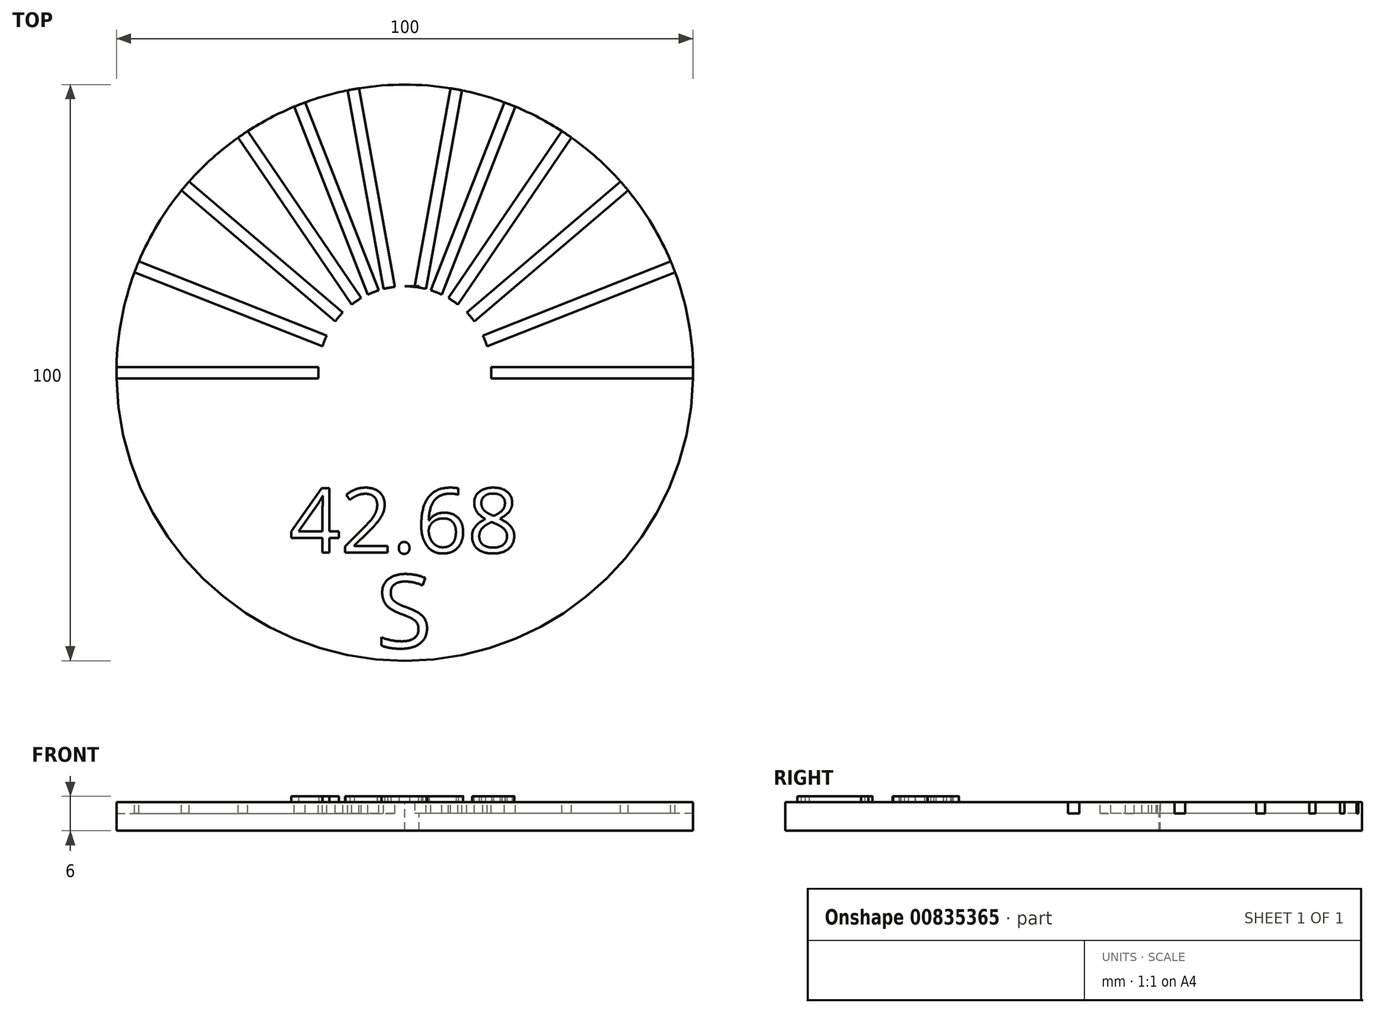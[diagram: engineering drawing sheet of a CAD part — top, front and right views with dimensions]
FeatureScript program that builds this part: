
annotation { "Feature Type Name" : "Feature", "Feature Type Description" : "" }
export const myFeature = defineFeature(function(context is Context, id is Id, definition is map)
    precondition{}
    {
        {
            var Q0;
            Q0=qCreatedBy(makeId("Top.planeOp"),FACE);
            var sketch = newSketch(context, id + "F0", { "sketchPlane" : qUnion([Q0])});
            skCircle(sketch, "E0", {"center": v(0, 0) * mm, "radius": 50 * mm});
            skSolve(sketch);
        }
        {
            var Q0;
            Q0 = qSketchRegion(id + "F0", true);
            extrude(context, id + "F1", {"entities" : qUnion([Q0]), "depth" : 5 * mm, "offsetDistance" : 25 * mm});
        }
        {
            var Q0;
            Q0=makeQuery(id+"F1.opExtrude","CAP_FACE",FACE,{"disambiguationData":[OSD([sQuery(id+"F0.wireOp",EDGE,"E0")])],"isStart":false});
            var sketch = newSketch(context, id + "F2", { "sketchPlane" : qUnion([Q0])});
            skCircle(sketch, "E1", {"center": v(0, 0) * mm, "radius": 15 * mm});
            skLineSegment(sketch, "E2", {"start": v(-50, 0) * mm, "end": v(0, 0) * mm, "construction": true});
            skLineSegment(sketch, "E3", {"start": v(-49.99, 1) * mm, "end": v(-14.97, 1) * mm});
            skLineSegment(sketch, "E4", {"start": v(-49.99, -1) * mm, "end": v(-14.97, -1) * mm});
            skPoint(sketch, "E5", {"position": v(-46.5, 18.38) * mm});
            skLineSegment(sketch, "E6", {"start": v(-46.5, 18.38) * mm, "end": v(0, 0) * mm, "construction": true});
            skLineSegment(sketch, "E7", {"start": v(-46.12, 19.3) * mm, "end": v(-13.55, 6.43) * mm});
            skLineSegment(sketch, "E8", {"start": v(-46.86, 17.45) * mm, "end": v(-14.29, 4.57) * mm});
            skLineSegment(sketch, "E9", {"start": v(-38.07, 32.42) * mm, "end": v(0, 0) * mm, "construction": true});
            skLineSegment(sketch, "E10", {"start": v(-37.4, 33.17) * mm, "end": v(-10.75, 10.47) * mm});
            skLineSegment(sketch, "E11", {"start": v(-38.7, 31.65) * mm, "end": v(-12.04, 8.94) * mm});
            skLineSegment(sketch, "E12", {"start": v(-28.05, 41.39) * mm, "end": v(0, 0) * mm, "construction": true});
            skLineSegment(sketch, "E13", {"start": v(-27.22, 41.94) * mm, "end": v(-7.57, 12.95) * mm});
            skLineSegment(sketch, "E14", {"start": v(-28.88, 40.82) * mm, "end": v(-9.23, 11.83) * mm});
            skLineSegment(sketch, "E15", {"start": v(-18.22, 46.56) * mm, "end": v(0, 0) * mm, "construction": true});
            skLineSegment(sketch, "E16", {"start": v(-19.15, 46.19) * mm, "end": v(-6.38, 13.57) * mm});
            skLineSegment(sketch, "E17", {"start": v(-17.28, 46.92) * mm, "end": v(-4.52, 14.3) * mm});
            skLineSegment(sketch, "E18", {"start": v(-8.94, 49.2) * mm, "end": v(0, 0) * mm, "construction": true});
            skLineSegment(sketch, "E19", {"start": v(-7.95, 49.36) * mm, "end": v(-1.7, 14.9) * mm});
            skLineSegment(sketch, "E20", {"start": v(-9.92, 49) * mm, "end": v(-3.66, 14.55) * mm});
            skLineSegment(sketch, "E21", {"start": v(50, 0) * mm, "end": v(0, 0) * mm, "construction": true});
            skLineSegment(sketch, "E22", {"start": v(49.99, 1) * mm, "end": v(14.97, 1) * mm});
            skLineSegment(sketch, "E23", {"start": v(49.99, -1) * mm, "end": v(14.97, -1) * mm});
            skLineSegment(sketch, "E24", {"start": v(46.5, 18.38) * mm, "end": v(0, 0) * mm, "construction": true});
            skLineSegment(sketch, "E25", {"start": v(46.86, 17.45) * mm, "end": v(14.29, 4.57) * mm});
            skLineSegment(sketch, "E26", {"start": v(46.12, 19.3) * mm, "end": v(13.55, 6.43) * mm});
            skLineSegment(sketch, "E27", {"start": v(38.07, 32.42) * mm, "end": v(0, 0) * mm, "construction": true});
            skLineSegment(sketch, "E28", {"start": v(38.7, 31.65) * mm, "end": v(12.04, 8.94) * mm});
            skLineSegment(sketch, "E29", {"start": v(37.4, 33.17) * mm, "end": v(10.75, 10.47) * mm});
            skLineSegment(sketch, "E30", {"start": v(28.05, 41.39) * mm, "end": v(0, 0) * mm, "construction": true});
            skLineSegment(sketch, "E31", {"start": v(28.88, 40.82) * mm, "end": v(9.23, 11.83) * mm});
            skLineSegment(sketch, "E32", {"start": v(27.22, 41.94) * mm, "end": v(7.57, 12.95) * mm});
            skLineSegment(sketch, "E33", {"start": v(18.22, 46.56) * mm, "end": v(0, 0) * mm, "construction": true});
            skLineSegment(sketch, "E34", {"start": v(19.15, 46.19) * mm, "end": v(6.38, 13.57) * mm});
            skLineSegment(sketch, "E35", {"start": v(17.28, 46.92) * mm, "end": v(4.52, 14.3) * mm});
            skLineSegment(sketch, "E36", {"start": v(8.94, 49.2) * mm, "end": v(0, 0) * mm, "construction": true});
            skLineSegment(sketch, "E37", {"start": v(9.92, 49) * mm, "end": v(3.66, 14.55) * mm});
            skLineSegment(sketch, "E38", {"start": v(7.95, 49.36) * mm, "end": v(1.7, 14.9) * mm});
            skSolve(sketch);
        }
        {
            var Q0;
            {var subQ0=sQuery(id+"F2.wireOp",EDGE,"E3");Q0=makeQuery(id+"F2.imprint","IMPRINT",FACE,{"disambiguationData":[TD([[makeQuery(id+"F2.imprint","IMPRINT",EDGE,{"derivedFrom":subQ0}),-1.0]])]});}
            var Q1;
            {var subQ0=sQuery(id+"F2.wireOp",EDGE,"E7");Q1=makeQuery(id+"F2.imprint","IMPRINT",FACE,{"disambiguationData":[TD([[makeQuery(id+"F2.imprint","IMPRINT",EDGE,{"derivedFrom":subQ0}),-1.0]])]});}
            var Q2;
            {var subQ0=sQuery(id+"F2.wireOp",EDGE,"E10");Q2=makeQuery(id+"F2.imprint","IMPRINT",FACE,{"disambiguationData":[TD([[makeQuery(id+"F2.imprint","IMPRINT",EDGE,{"derivedFrom":subQ0}),-1.0]])]});}
            var Q3;
            {var subQ0=sQuery(id+"F2.wireOp",EDGE,"E13");Q3=makeQuery(id+"F2.imprint","IMPRINT",FACE,{"disambiguationData":[TD([[makeQuery(id+"F2.imprint","IMPRINT",EDGE,{"derivedFrom":subQ0}),-1.0]])]});}
            var Q4;
            {var subQ0=sQuery(id+"F2.wireOp",EDGE,"E16");Q4=makeQuery(id+"F2.imprint","IMPRINT",FACE,{"disambiguationData":[TD([[makeQuery(id+"F2.imprint","IMPRINT",EDGE,{"derivedFrom":subQ0}),1.0]])]});}
            var Q5;
            {var subQ0=sQuery(id+"F2.wireOp",EDGE,"E19");Q5=makeQuery(id+"F2.imprint","IMPRINT",FACE,{"disambiguationData":[TD([[makeQuery(id+"F2.imprint","IMPRINT",EDGE,{"derivedFrom":subQ0}),-1.0]])]});}
            var Q6;
            {var subQ0=sQuery(id+"F2.wireOp",EDGE,"cLizcYDV-IRRK-Rsa2-aBVT-mdBlfsuyFpmo");Q6=makeQuery(id+"F2.imprint","IMPRINT",FACE,{"disambiguationData":[TD([[makeQuery(id+"F2.imprint","IMPRINT",EDGE,{"derivedFrom":subQ0}),1.0]])]});}
            var Q7;
            {var subQ0=sQuery(id+"F2.wireOp",EDGE,"E37");Q7=makeQuery(id+"F2.imprint","IMPRINT",FACE,{"disambiguationData":[TD([[makeQuery(id+"F2.imprint","IMPRINT",EDGE,{"derivedFrom":subQ0}),-1.0]])]});}
            var Q8;
            {var subQ0=sQuery(id+"F2.wireOp",EDGE,"E34");Q8=makeQuery(id+"F2.imprint","IMPRINT",FACE,{"disambiguationData":[TD([[makeQuery(id+"F2.imprint","IMPRINT",EDGE,{"derivedFrom":subQ0}),-1.0]])]});}
            var Q9;
            {var subQ0=sQuery(id+"F2.wireOp",EDGE,"E31");Q9=makeQuery(id+"F2.imprint","IMPRINT",FACE,{"disambiguationData":[TD([[makeQuery(id+"F2.imprint","IMPRINT",EDGE,{"derivedFrom":subQ0}),-1.0]])]});}
            var Q10;
            {var subQ0=sQuery(id+"F2.wireOp",EDGE,"E28");Q10=makeQuery(id+"F2.imprint","IMPRINT",FACE,{"disambiguationData":[TD([[makeQuery(id+"F2.imprint","IMPRINT",EDGE,{"derivedFrom":subQ0}),-1.0]])]});}
            var Q11;
            {var subQ0=sQuery(id+"F2.wireOp",EDGE,"E25");Q11=makeQuery(id+"F2.imprint","IMPRINT",FACE,{"disambiguationData":[TD([[makeQuery(id+"F2.imprint","IMPRINT",EDGE,{"derivedFrom":subQ0}),-1.0]])]});}
            var Q12;
            {var subQ0=sQuery(id+"F2.wireOp",EDGE,"E22");Q12=makeQuery(id+"F2.imprint","IMPRINT",FACE,{"disambiguationData":[TD([[makeQuery(id+"F2.imprint","IMPRINT",EDGE,{"derivedFrom":subQ0}),1.0]])]});}
            extrude(context, id + "F3", {"entities" : qUnion([Q0, Q1, Q2, Q3, Q4, Q5, Q6, Q7, Q8, Q9, Q10, Q11, Q12]), "operationType" : NewBodyOperationType.REMOVE, "oppositeDirection" : true, "depth" : 2 * mm, "offsetDistance" : 25 * mm});
        }
        {
            var Q0;
            Q0=makeQuery(id+"F1.opExtrude","CAP_FACE",FACE,{"disambiguationData":[OSD([sQuery(id+"F0.wireOp",EDGE,"E0")])],"isStart":false});
            var sketch = newSketch(context, id + "F4", { "sketchPlane" : qUnion([Q0])});
            skCircle(sketch, "E39", {"center": v(0, 0) * mm, "radius": 15 * mm});
            skSolve(sketch);
        }
        {
            var Q0;
            {var subQ0=sQuery(id+"F0.wireOp",EDGE,"E0");Q0=makeQuery(id+"FESnY8lzPuoSr7a_1.boolean.opBoolean","SPLIT",FACE,{"disambiguationData":[TD([makeQuery(id+"F3.boolean.opBoolean","COPY",FACE,{"derivedFrom":makeQuery(id+"F3.opExtrude","SWEPT_FACE",FACE,{"disambiguationData":[OSD([sQuery(id+"F2.wireOp",EDGE,"E4")])]})})])],"derivedFrom":makeQuery(id+"F1.opExtrude","CAP_FACE",FACE,{"disambiguationData":[OSD([subQ0])],"isStart":false})});}
            var sketch = newSketch(context, id + "F5", { "sketchPlane" : qUnion([Q0])});
            skText(sketch, "E40", { "text": "S", "fontName": "OpenSans-Regular.ttf"});
            const initialGuessF5  = {"E40": [-0.005, -0.04773, 1, 0, 0.01273]};
            skSetInitialGuess(sketch, initialGuessF5);
            skSolve(sketch);
        }
        {
            var Q0;
            Q0 = qSketchRegion(id + "F5", true);
            extrude(context, id + "F6", {"entities" : qUnion([Q0]), "operationType" : NewBodyOperationType.ADD, "depth" : 1 * mm, "offsetDistance" : 25 * mm});
        }
        {
            var Q0;
            {var subQ0=sQuery(id+"F0.wireOp",EDGE,"E0");Q0=makeQuery(id+"FESnY8lzPuoSr7a_1.boolean.opBoolean","SPLIT",FACE,{"disambiguationData":[TD([makeQuery(id+"F3.boolean.opBoolean","COPY",FACE,{"derivedFrom":makeQuery(id+"F3.opExtrude","SWEPT_FACE",FACE,{"disambiguationData":[OSD([sQuery(id+"F2.wireOp",EDGE,"E4")])]})})])],"derivedFrom":makeQuery(id+"F1.opExtrude","CAP_FACE",FACE,{"disambiguationData":[OSD([subQ0])],"isStart":false})});}
            var sketch = newSketch(context, id + "F7", { "sketchPlane" : qUnion([Q0])});
            skText(sketch, "E41", { "text": "42.68", "fontName": "OpenSans-Regular.ttf"});
            const initialGuessF7  = {"E41": [-0.02, -0.03122, 1, 0, 0.01122]};
            skSetInitialGuess(sketch, initialGuessF7);
            skSolve(sketch);
        }
        {
            var Q0;
            Q0 = qSketchRegion(id + "F7", true);
            extrude(context, id + "F8", {"entities" : qUnion([Q0]), "operationType" : NewBodyOperationType.ADD, "depth" : 1 * mm, "offsetDistance" : 25 * mm});
        }
        {
            var Q0;
            {var subQ0=sQuery(id+"F4.wireOp",EDGE,"E39");var subQ18=makeQuery(id+"F4.imprint","INTERSECT",VERTEX,{"derivedFrom":[makeQuery(id+"F3.boolean.opBoolean","COPY",EDGE,{"derivedFrom":makeQuery(id+"F3.opExtrude","CAP_EDGE",EDGE,{"disambiguationData":[OSD([sQuery(id+"F2.wireOp",EDGE,"E22")])],"isStart":true})}),subQ0]});Q0=makeQuery(id+"F4.imprint","IMPRINT",FACE,{"disambiguationData":[TD([[makeQuery(id+"F4.imprint","IMPRINT",EDGE,{"disambiguationData":[TD([[subQ18,-1.0]])],"derivedFrom":subQ0}),1.0]])]});}
            var sketch = newSketch(context, id + "F9", { "sketchPlane" : qUnion([Q0])});
            skLineSegment(sketch, "E42.bottom", {"start": v(2.5, -15) * mm, "end": v(-2.5, -15) * mm});
            skLineSegment(sketch, "E42.top", {"start": v(2.5, 15) * mm, "end": v(-2.5, 15) * mm});
            skLineSegment(sketch, "E42.left", {"start": v(2.5, -15) * mm, "end": v(2.5, 15) * mm});
            skLineSegment(sketch, "E42.right", {"start": v(-2.5, -15) * mm, "end": v(-2.5, 15) * mm});
            skPoint(sketch, "E42.middle", {"position": v(0, 0) * mm});
            skSolve(sketch);
        }
        {
            var Q0;
            {var subQ0=sQuery(id+"F4.wireOp",EDGE,"E39");var subQ9=sQuery(id+"F9.wireOp",EDGE,"E42.left");var subQ12=makeQuery(id+"F4.imprint","IMPRINT",EDGE,{"disambiguationData":[TD([[makeQuery(id+"F4.imprint","INTERSECT",VERTEX,{"derivedFrom":[makeQuery(id+"F3.boolean.opBoolean","COPY",EDGE,{"derivedFrom":makeQuery(id+"F3.opExtrude","CAP_EDGE",EDGE,{"disambiguationData":[OSD([sQuery(id+"F2.wireOp",EDGE,"E4")])],"isStart":true})}),subQ0]}),-1.0]])],"derivedFrom":subQ0});var subQ15=makeQuery(id+"F9.imprint","INTERSECT",VERTEX,{"derivedFrom":[subQ12,subQ9]});Q0=makeQuery(id+"F9.imprint","IMPRINT",FACE,{"disambiguationData":[TD([[makeQuery(id+"F9.imprint","IMPRINT",EDGE,{"disambiguationData":[TD([[subQ15,-1.0]])],"derivedFrom":subQ9}),1.0]])]});}
            extrude(context, id + "F10", {"entities" : qUnion([Q0]), "operationType" : NewBodyOperationType.REMOVE, "endBound" : BoundingType.THROUGH_ALL, "oppositeDirection" : true, "depth" : 25 * mm, "offsetDistance" : 25 * mm});
        }
    });
